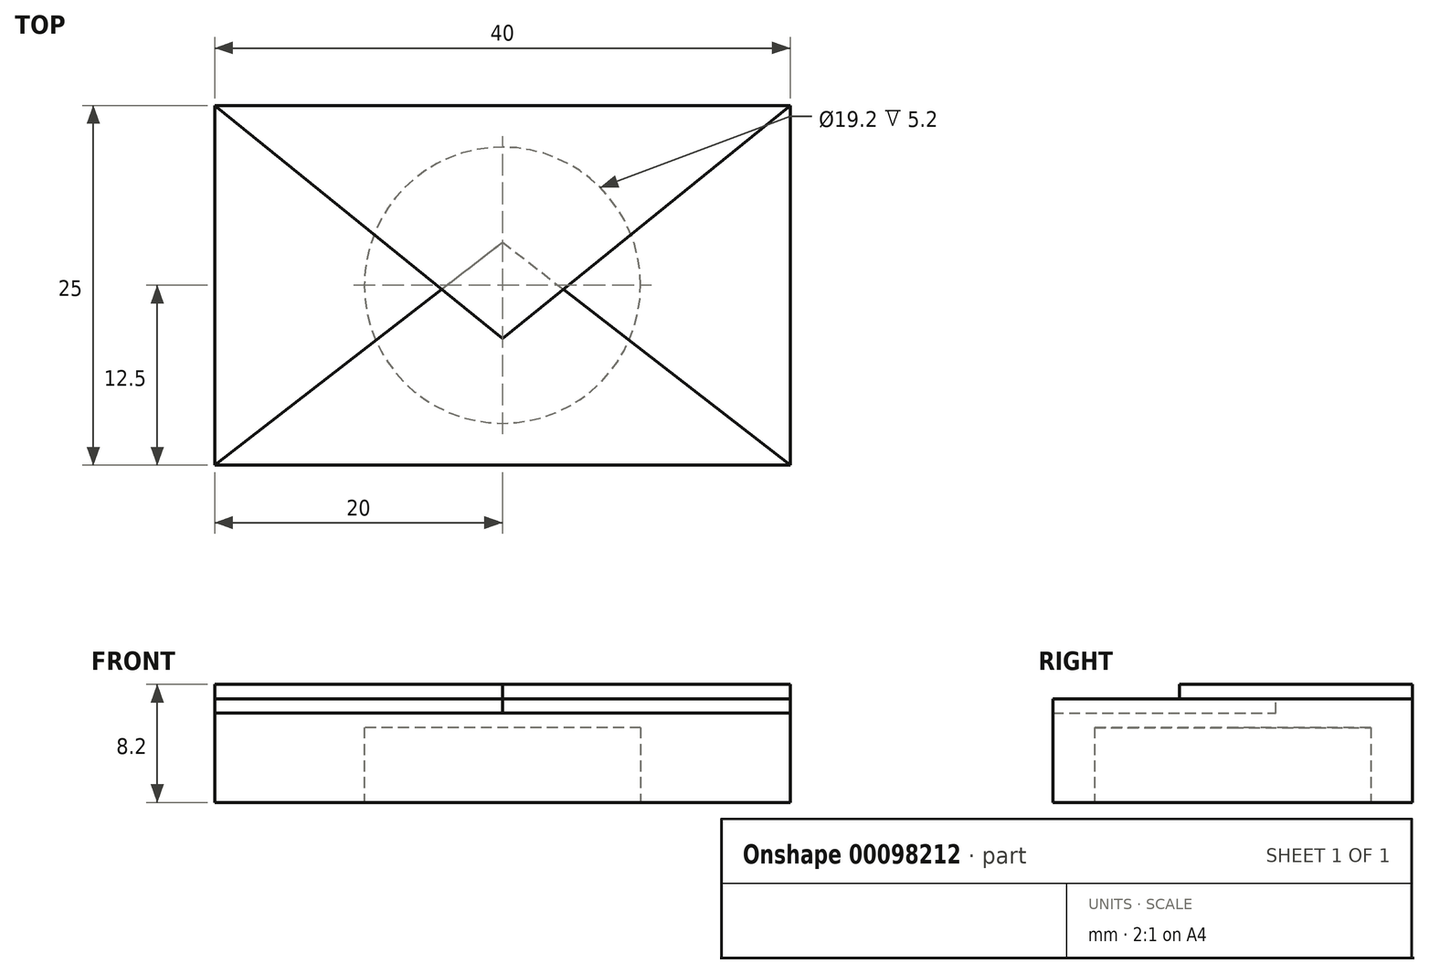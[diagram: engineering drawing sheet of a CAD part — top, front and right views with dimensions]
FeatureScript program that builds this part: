
annotation { "Feature Type Name" : "Feature", "Feature Type Description" : "" }
export const myFeature = defineFeature(function(context is Context, id is Id, definition is map)
    precondition{}
    {
        {
            var Q0;
            Q0=qCreatedBy(makeId("Top.planeOp"),FACE);
            var sketch = newSketch(context, id + "F0", { "sketchPlane" : qUnion([Q0])});
            skCircle(sketch, "E0", {"center": v(0, 0) * mm, "radius": 9.6 * mm});
            skCircle(sketch, "E1.0", {"center": v(0, 0) * mm, "radius": 11.6 * mm});
            skSolve(sketch);
        }
        {
            var Q0;
            Q0=qSketchRegion(id+"F0",true);
            extrude(context, id + "F1", {"entities" : qUnion([Q0]), "depth" : 5.2 * mm});
        }
        {
            var Q0;
            Q0=makeQuery(id+"F1.opExtrude","CAP_FACE",FACE,{"disambiguationData":[OSD([sQuery(id+"F0.wireOp",EDGE,"E0"),sQuery(id+"F0.wireOp",EDGE,"E1.0")])],"isStart":false});
            var sketch = newSketch(context, id + "F2", { "sketchPlane" : qUnion([Q0])});
            skSolve(sketch);
        }
        {
            var Q0;
            Q0=makeQuery(id+"F2.imprint","IMPRINT",FACE,{"disambiguationData":[TD([[makeQuery(id+"F2.imprint","IMPRINT",EDGE,{"derivedFrom":makeQuery(id+"F1.opExtrude","CAP_EDGE",EDGE,{"disambiguationData":[OSD([sQuery(id+"F0.wireOp",EDGE,"E0")])],"isStart":false})}),1.0]])]});
            var Q1;
            Q1=makeQuery(id+"F2.imprint","IMPRINT",FACE,{"disambiguationData":[TD([[makeQuery(id+"F2.imprint","IMPRINT",EDGE,{"derivedFrom":makeQuery(id+"F1.opExtrude","CAP_EDGE",EDGE,{"disambiguationData":[OSD([sQuery(id+"F0.wireOp",EDGE,"E0")])],"isStart":false})}),-1.0]])]});
            extrude(context, id + "F3", {"entities" : qUnion([Q0, Q1]), "operationType" : NewBodyOperationType.ADD, "depth" : 2 * mm});
        }
        {
            var Q0;
            Q0=makeQuery(id+"F3.opExtrude","CAP_FACE",FACE,{"disambiguationData":[OSD([sQuery(id+"F0.wireOp",EDGE,"E1.0")])],"isStart":false});
            var sketch = newSketch(context, id + "F4", { "sketchPlane" : qUnion([Q0])});
            skLineSegment(sketch, "E2.bottom", {"start": v(-20, 12.5) * mm, "end": v(20, 12.5) * mm});
            skLineSegment(sketch, "E2.top", {"start": v(-20, -12.5) * mm, "end": v(20, -12.5) * mm});
            skLineSegment(sketch, "E2.left", {"start": v(-20, 12.5) * mm, "end": v(-20, -12.5) * mm});
            skLineSegment(sketch, "E2.right", {"start": v(20, 12.5) * mm, "end": v(20, -12.5) * mm});
            skPoint(sketch, "E2.middle", {"position": v(0, 0) * mm});
            skSolve(sketch);
        }
        {
            var Q0;
            Q0=makeQuery(id+"F4.imprint","IMPRINT",FACE,{"disambiguationData":[TD([[makeQuery(id+"F4.imprint","IMPRINT",EDGE,{"derivedFrom":sQuery(id+"F4.wireOp",EDGE,"E2.bottom")}),-1.0]])]});
            extrude(context, id + "F5", {"entities" : qUnion([Q0]), "operationType" : NewBodyOperationType.ADD, "oppositeDirection" : true, "depth" : 7.2 * mm});
        }
        {
            var Q0;
            {var subQ0=sQuery(id+"F0.wireOp",EDGE,"E1.0");Q0=makeQuery(id+"F5.boolean.opBoolean","MERGE",FACE,{"derivedFrom":[makeQuery(id+"F3.opExtrude","CAP_FACE",FACE,{"disambiguationData":[OSD([subQ0])],"isStart":false}),makeQuery(id+"F5.opExtrude","CAP_FACE",FACE,{"disambiguationData":[OSD([subQ0,sQuery(id+"F4.wireOp",EDGE,"E2.bottom"),sQuery(id+"F4.wireOp",EDGE,"E2.top"),sQuery(id+"F4.wireOp",EDGE,"E2.left"),sQuery(id+"F4.wireOp",EDGE,"E2.right")])],"isStart":true})]});}
            var sketch = newSketch(context, id + "F6", { "sketchPlane" : qUnion([Q0])});
            skLineSegment(sketch, "E3", {"start": v(-20, -12.5) * mm, "end": v(0, 3) * mm});
            skLineSegment(sketch, "E4", {"start": v(0, 3) * mm, "end": v(20, -12.5) * mm});
            skSolve(sketch);
        }
        {
            var Q0;
            Q0 = qSketchRegion(id + "F6", true);
            var Q1;
            Q1=makeQuery(id+"F6.imprint","IMPRINT",FACE,{"disambiguationData":[TD([[makeQuery(id+"F6.imprint","IMPRINT",EDGE,{"derivedFrom":sQuery(id+"F6.wireOp",EDGE,"E3")}),-1.0]])]});
            extrude(context, id + "F7", {"entities" : qUnion([Q0, Q1]), "operationType" : NewBodyOperationType.REMOVE, "oppositeDirection" : true, "depth" : 1 * mm});
        }
        {
            var Q0;
            {var subQ0=sQuery(id+"F0.wireOp",EDGE,"E1.0");Q0=makeQuery(id+"F5.boolean.opBoolean","MERGE",FACE,{"derivedFrom":[makeQuery(id+"F3.opExtrude","CAP_FACE",FACE,{"disambiguationData":[OSD([subQ0])],"isStart":false}),makeQuery(id+"F5.opExtrude","CAP_FACE",FACE,{"disambiguationData":[OSD([subQ0,sQuery(id+"F4.wireOp",EDGE,"E2.bottom"),sQuery(id+"F4.wireOp",EDGE,"E2.top"),sQuery(id+"F4.wireOp",EDGE,"E2.left"),sQuery(id+"F4.wireOp",EDGE,"E2.right")])],"isStart":true})]});}
            var sketch = newSketch(context, id + "F8", { "sketchPlane" : qUnion([Q0])});
            skLineSegment(sketch, "E5", {"start": v(-20, 12.5) * mm, "end": v(0, -3.7) * mm});
            skLineSegment(sketch, "E6", {"start": v(0, -3.7) * mm, "end": v(20, 12.5) * mm});
            skSolve(sketch);
        }
        {
            var Q0;
            Q0 = qSketchRegion(id + "F8", true);
            var Q1;
            {var subQ0=makeQuery(id+"F5.opExtrude","CAP_EDGE",EDGE,{"disambiguationData":[OSD([sQuery(id+"F4.wireOp",EDGE,"E2.bottom")])],"isStart":true});Q1=makeQuery(id+"F8.imprint","IMPRINT",FACE,{"disambiguationData":[TD([[makeQuery(id+"F8.imprint","IMPRINT",EDGE,{"derivedFrom":subQ0}),-1.0]])]});}
            var Q2;
            {var subQ0=sQuery(id+"F8.wireOp",EDGE,"E6");var subQ1=sQuery(id+"F8.wireOp",EDGE,"E5");var subQ2=makeQuery(id+"F8.imprint","INTERSECT",VERTEX,{"derivedFrom":[subQ1,subQ0]});Q2=makeQuery(id+"F8.imprint","IMPRINT",FACE,{"disambiguationData":[TD([[makeQuery(id+"F8.imprint","IMPRINT",EDGE,{"disambiguationData":[TD([[subQ2,1.0]])],"derivedFrom":subQ1}),1.0]])]});}
            extrude(context, id + "F9", {"entities" : qUnion([Q0, Q1, Q2]), "operationType" : NewBodyOperationType.ADD, "depth" : 1 * mm});
        }
    });
